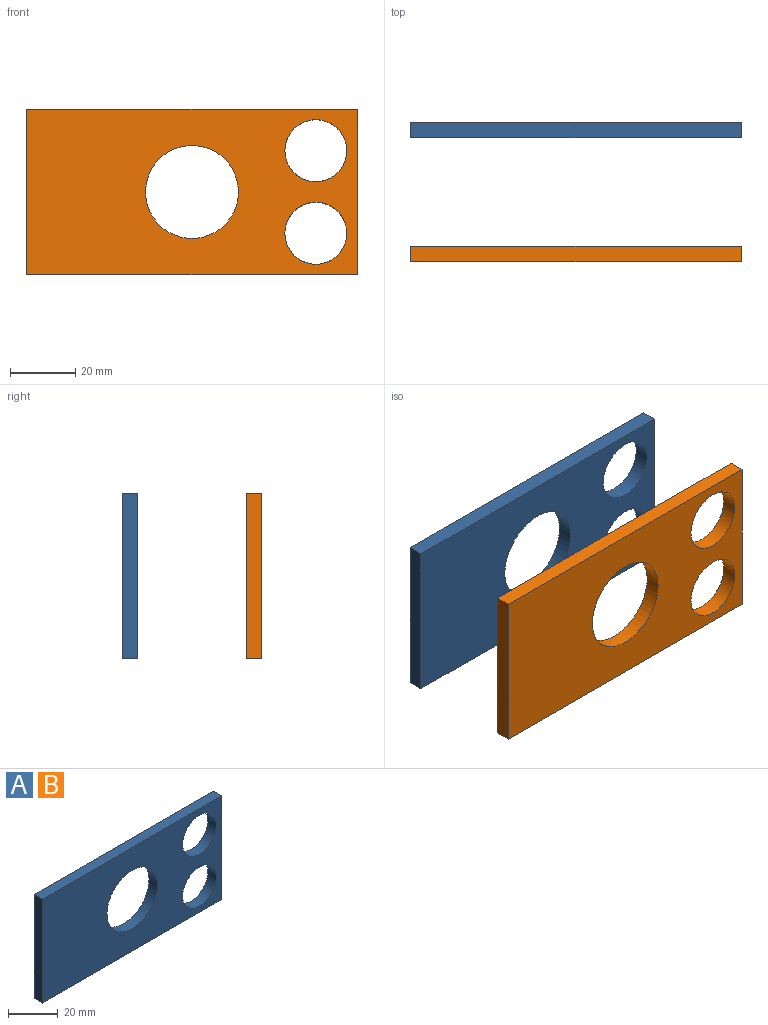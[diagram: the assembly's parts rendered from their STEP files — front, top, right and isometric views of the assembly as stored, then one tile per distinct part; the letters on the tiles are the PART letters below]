
ASSEMBLY  parts=2 mates=1
PART A: 9 faces, bbox 101.6x4.8x50.8 mm
  f0: plane 101.6x4.76mm, normal (0,0,1), area 483.9mm2, adj f1,f4,f5,f6
  f1: plane 50.8x4.76mm, normal (-1,0,0), area 241.9mm2, adj f0,f2,f5,f6
  f2: plane 101.6x4.76mm, normal (0,0,-1), area 483.9mm2, adj f1,f4,f5,f6
  f3: cylinder r=14.29mm len=28.58mm, axis (0,1,0), area 427.5mm2, adj f5,f6
  f4: plane 50.8x4.76mm, normal (1,0,0), area 241.9mm2, adj f0,f2,f5,f6
  f5: plane 101.6x50.8mm, normal (0,-1,0), area 3949.9mm2, adj f0,f1,f2,f3,f4,f7,f8
  f6: plane 101.6x50.8mm, normal (0,1,0), area 3949.9mm2, adj f0,f1,f2,f3,f4,f7,f8
  f7: cylinder r=9.53mm len=19.05mm, axis (0,1,0), area 285mm2, adj f5,f6
  f8: cylinder r=9.53mm len=19.05mm, axis (0,1,0), area 285mm2, adj f5,f6
PART B: same geometry as A
PLACE A t=(0,38.1,0)mm
PLACE B at identity
MATE fastened A.f3 <-> B.f3  axis (0,1,0) through (0,40.48,0)mm
